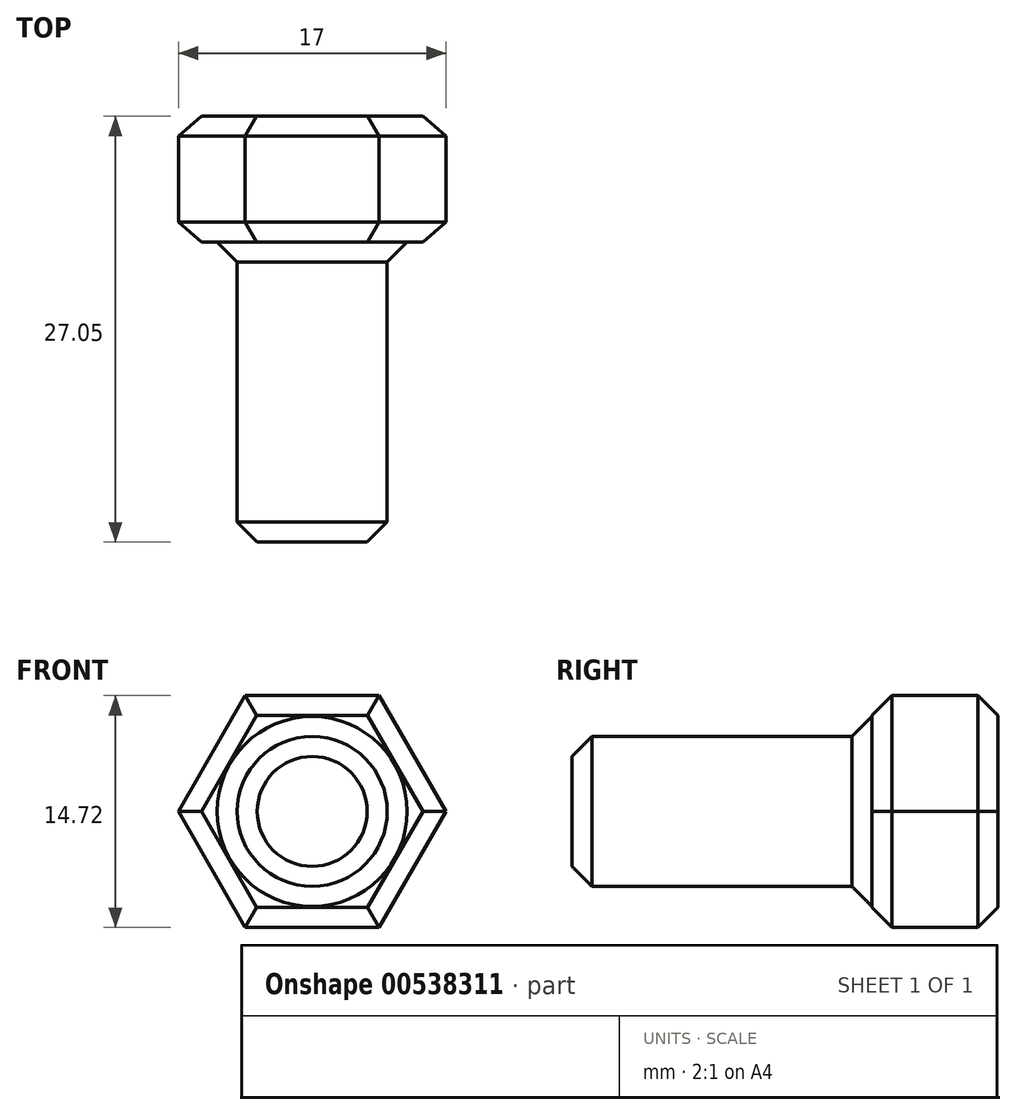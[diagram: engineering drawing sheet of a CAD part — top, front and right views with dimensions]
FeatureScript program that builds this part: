
annotation { "Feature Type Name" : "Feature", "Feature Type Description" : "" }
export const myFeature = defineFeature(function(context is Context, id is Id, definition is map)
    precondition{}
    {
        {
            var Q0;
            Q0=qCreatedBy(makeId("Front.planeOp"),FACE);
            var sketch = newSketch(context, id + "F0", { "sketchPlane" : qUnion([Q0])});
            skCircle(sketch, "E0.cCircle", {"center": v(0, 0) * mm, "radius": 8.5 * mm, "construction": true});
            skLineSegment(sketch, "E0.0", {"start": v(8.5, 0) * mm, "end": v(4.25, -7.36) * mm});
            skLineSegment(sketch, "E0.1", {"start": v(4.25, -7.36) * mm, "end": v(-4.25, -7.36) * mm});
            skLineSegment(sketch, "E0.2", {"start": v(-4.25, -7.36) * mm, "end": v(-8.5, 0) * mm});
            skLineSegment(sketch, "E0.3", {"start": v(-8.5, 0) * mm, "end": v(-4.25, 7.36) * mm});
            skLineSegment(sketch, "E0.4", {"start": v(-4.25, 7.36) * mm, "end": v(4.25, 7.36) * mm});
            skLineSegment(sketch, "E0.5", {"start": v(4.25, 7.36) * mm, "end": v(8.5, 0) * mm});
            skSolve(sketch);
        }
        {
            var Q0;
            Q0 = qSketchRegion(id + "F0", true);
            extrude(context, id + "F1", {"entities" : qUnion([Q0]), "depth" : 8 * mm, "offsetDistance" : 25.4 * mm});
        }
        {
            var Q0;
            Q0=makeQuery(id+"F1.opExtrude","CAP_FACE",FACE,{"disambiguationData":[OSD([sQuery(id+"F0.wireOp",EDGE,"E0.0"),sQuery(id+"F0.wireOp",EDGE,"E0.1"),sQuery(id+"F0.wireOp",EDGE,"E0.2"),sQuery(id+"F0.wireOp",EDGE,"E0.3"),sQuery(id+"F0.wireOp",EDGE,"E0.4"),sQuery(id+"F0.wireOp",EDGE,"E0.5")])],"isStart":false});
            var sketch = newSketch(context, id + "F2", { "sketchPlane" : qUnion([Q0])});
            skCircle(sketch, "E1", {"center": v(0, 0) * mm, "radius": 4.76 * mm});
            skSolve(sketch);
        }
        {
            var Q0;
            Q0 = qSketchRegion(id + "F2", true);
            extrude(context, id + "F3", {"entities" : qUnion([Q0]), "operationType" : NewBodyOperationType.ADD, "depth" : 19.05 * mm, "offsetDistance" : 25.4 * mm});
        }
        {
            var Q0;
            Q0=makeQuery(id+"F3.opExtrude","CAP_EDGE",EDGE,{"disambiguationData":[OSD([sQuery(id+"F2.wireOp",EDGE,"E1")])],"isStart":false});
            var Q1;
            Q1=makeQuery(id+"F1.opExtrude","CAP_EDGE",EDGE,{"disambiguationData":[OSD([sQuery(id+"F0.wireOp",EDGE,"E0.5")])],"isStart":true});
            var Q2;
            Q2=makeQuery(id+"F1.opExtrude","CAP_EDGE",EDGE,{"disambiguationData":[OSD([sQuery(id+"F0.wireOp",EDGE,"E0.1")])],"isStart":true});
            var Q3;
            Q3=makeQuery(id+"F1.opExtrude","CAP_EDGE",EDGE,{"disambiguationData":[OSD([sQuery(id+"F0.wireOp",EDGE,"E0.0")])],"isStart":true});
            var Q4;
            Q4=makeQuery(id+"F1.opExtrude","CAP_EDGE",EDGE,{"disambiguationData":[OSD([sQuery(id+"F0.wireOp",EDGE,"E0.2")])],"isStart":true});
            var Q5;
            Q5=makeQuery(id+"F1.opExtrude","CAP_EDGE",EDGE,{"disambiguationData":[OSD([sQuery(id+"F0.wireOp",EDGE,"E0.3")])],"isStart":true});
            var Q6;
            Q6=makeQuery(id+"F1.opExtrude","CAP_EDGE",EDGE,{"disambiguationData":[OSD([sQuery(id+"F0.wireOp",EDGE,"E0.4")])],"isStart":true});
            var Q7;
            Q7=makeQuery(id+"F1.opExtrude","CAP_EDGE",EDGE,{"disambiguationData":[OSD([sQuery(id+"F0.wireOp",EDGE,"E0.5")])],"isStart":false});
            var Q8;
            Q8=makeQuery(id+"F1.opExtrude","CAP_EDGE",EDGE,{"disambiguationData":[OSD([sQuery(id+"F0.wireOp",EDGE,"E0.0")])],"isStart":false});
            var Q9;
            Q9=makeQuery(id+"F3.opExtrude","SWEPT_FACE",FACE,{"disambiguationData":[OSD([sQuery(id+"F2.wireOp",EDGE,"E1")])]});
            var Q10;
            Q10=makeQuery(id+"F1.opExtrude","CAP_EDGE",EDGE,{"disambiguationData":[OSD([sQuery(id+"F0.wireOp",EDGE,"E0.4")])],"isStart":false});
            var Q11;
            Q11=makeQuery(id+"F1.opExtrude","CAP_EDGE",EDGE,{"disambiguationData":[OSD([sQuery(id+"F0.wireOp",EDGE,"E0.3")])],"isStart":false});
            var Q12;
            Q12=makeQuery(id+"F1.opExtrude","CAP_EDGE",EDGE,{"disambiguationData":[OSD([sQuery(id+"F0.wireOp",EDGE,"E0.1")])],"isStart":false});
            var Q13;
            Q13=makeQuery(id+"F1.opExtrude","CAP_EDGE",EDGE,{"disambiguationData":[OSD([sQuery(id+"F0.wireOp",EDGE,"E0.2")])],"isStart":false});
            chamfer(context, id + "F4", {"entities" : qUnion([Q0, Q1, Q2, Q3, Q4, Q5, Q6, Q7, Q8, Q9, Q10, Q11, Q12, Q13]), "width" : 1.27 * mm, "tangentPropagation" : true});
        }
    });
